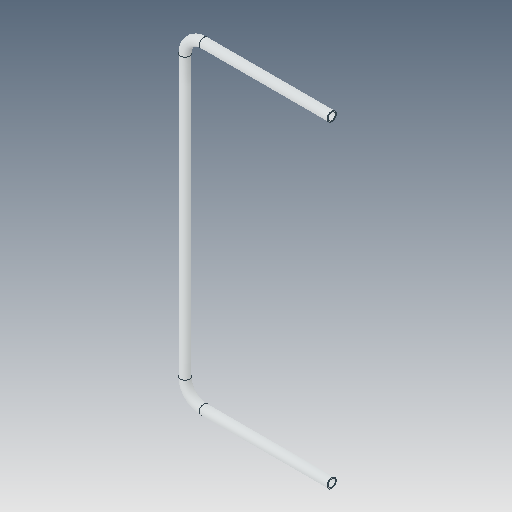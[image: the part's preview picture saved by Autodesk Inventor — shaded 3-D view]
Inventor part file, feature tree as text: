
AUTODESK INVENTOR PART (.ipt)
format: ipt  version: 2023.5 (Build 275446000, 446)  size: 99,840 bytes
history: native  units: in
note: dims shown in document units (in); Inventor stores cm internally (conversion verified against a paired STEP export)
features: sweep x1
ambient origin geometry x8: Origin, YZ Plane, XZ Plane, XY Plane, X Axis, Y Axis, Z Axis, Center Point
bodies: Solid1 (feature_tree)
feature tree (1):
  sweep  "Sweep1"
